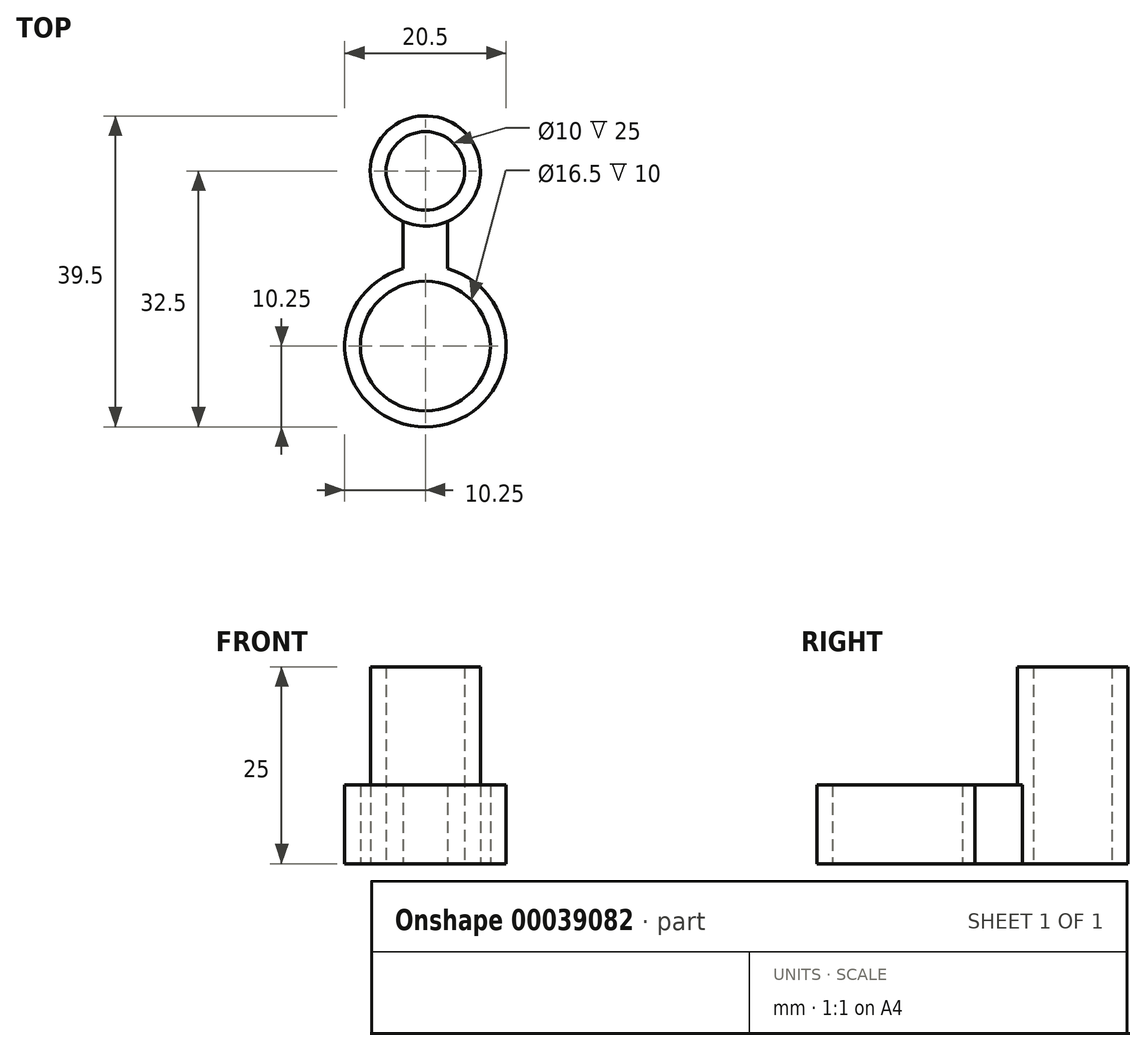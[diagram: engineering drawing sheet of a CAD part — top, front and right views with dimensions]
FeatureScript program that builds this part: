
annotation { "Feature Type Name" : "Feature", "Feature Type Description" : "" }
export const myFeature = defineFeature(function(context is Context, id is Id, definition is map)
    precondition{}
    {
        {
            var Q0;
            Q0=qCreatedBy(makeId("Top.planeOp"),FACE);
            var sketch = newSketch(context, id + "F0", { "sketchPlane" : qUnion([Q0])});
            skCircle(sketch, "E0", {"center": v(0, 0) * mm, "radius": 8.25 * mm});
            skCircle(sketch, "E1", {"center": v(0, 22.25) * mm, "radius": 5 * mm});
            skCircle(sketch, "E2.0", {"center": v(0, 0) * mm, "radius": 10.25 * mm});
            skCircle(sketch, "E3.0", {"center": v(0, 22.25) * mm, "radius": 7 * mm});
            skLineSegment(sketch, "E4", {"start": v(0, 0) * mm, "end": v(0, 8.25) * mm, "construction": true});
            skLineSegment(sketch, "E5", {"start": v(0, 10.25) * mm, "end": v(0, 8.25) * mm, "construction": true});
            skLineSegment(sketch, "E6", {"start": v(0, 17.25) * mm, "end": v(0, 15.25) * mm, "construction": true});
            skLineSegment(sketch, "E7", {"start": v(0, 17.25) * mm, "end": v(0, 22.25) * mm, "construction": true});
            skLineSegment(sketch, "E8", {"start": v(0, 17.25) * mm, "end": v(2.84, 17.25) * mm});
            skLineSegment(sketch, "E9", {"start": v(0, 17.25) * mm, "end": v(-2.84, 17.25) * mm});
            skLineSegment(sketch, "E10", {"start": v(2.84, 17.25) * mm, "end": v(2.84, 8.25) * mm});
            skLineSegment(sketch, "E11", {"start": v(2.84, 8.25) * mm, "end": v(0, 8.25) * mm});
            skLineSegment(sketch, "E12", {"start": v(-2.84, 17.25) * mm, "end": v(-2.84, 8.25) * mm});
            skLineSegment(sketch, "E13", {"start": v(-2.84, 8.25) * mm, "end": v(0, 8.25) * mm});
            skSolve(sketch);
        }
        {
            var Q0;
            Q0=makeQuery(id+"F0.imprint","IMPRINT",FACE,{"disambiguationData":[TD([[makeQuery(id+"F0.imprint","IMPRINT",EDGE,{"derivedFrom":sQuery(id+"F0.wireOp",EDGE,"E1")}),-1.0]])]});
            var Q1;
            {var subQ6=sQuery(id+"F0.wireOp",EDGE,"E8");Q1=makeQuery(id+"F0.imprint","IMPRINT",FACE,{"disambiguationData":[TD([[makeQuery(id+"F0.imprint","IMPRINT",EDGE,{"derivedFrom":subQ6}),-1.0]])]});}
            var Q2;
            {var subQ3=sQuery(id+"F0.wireOp",EDGE,"E2.0");var subQ5=sQuery(id+"F0.wireOp",EDGE,"E10");var subQ7=makeQuery(id+"F0.imprint","INTERSECT",VERTEX,{"derivedFrom":[subQ3,subQ5]});Q2=makeQuery(id+"F0.imprint","IMPRINT",FACE,{"disambiguationData":[TD([[makeQuery(id+"F0.imprint","IMPRINT",EDGE,{"disambiguationData":[TD([[subQ7,-1.0]])],"derivedFrom":subQ3}),-1.0]])]});}
            var Q3;
            {var subQ6=sQuery(id+"F0.wireOp",EDGE,"E11");Q3=makeQuery(id+"F0.imprint","IMPRINT",FACE,{"disambiguationData":[TD([[makeQuery(id+"F0.imprint","IMPRINT",EDGE,{"derivedFrom":subQ6}),-1.0]])]});}
            var Q4;
            Q4=makeQuery(id+"F0.imprint","IMPRINT",FACE,{"disambiguationData":[TD([[makeQuery(id+"F0.imprint","IMPRINT",EDGE,{"derivedFrom":sQuery(id+"F0.wireOp",EDGE,"E0")}),-1.0]])]});
            extrude(context, id + "F1", {"entities" : qUnion([Q0, Q1, Q2, Q3, Q4]), "depth" : 10 * mm});
        }
        {
            var Q0;
            Q0=makeQuery(id+"F0.imprint","IMPRINT",FACE,{"disambiguationData":[TD([[makeQuery(id+"F0.imprint","IMPRINT",EDGE,{"derivedFrom":sQuery(id+"F0.wireOp",EDGE,"E1")}),-1.0]])]});
            var Q1;
            {var subQ6=sQuery(id+"F0.wireOp",EDGE,"E8");Q1=makeQuery(id+"F0.imprint","IMPRINT",FACE,{"disambiguationData":[TD([[makeQuery(id+"F0.imprint","IMPRINT",EDGE,{"derivedFrom":subQ6}),-1.0]])]});}
            extrude(context, id + "F2", {"entities" : qUnion([Q0, Q1]), "operationType" : NewBodyOperationType.ADD, "depth" : 25 * mm});
        }
    });
